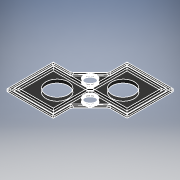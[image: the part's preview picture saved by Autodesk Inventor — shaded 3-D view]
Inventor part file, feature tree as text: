
AUTODESK INVENTOR PART (.ipt)
format: ipt  version: 2018 (Build 220112000, 112)  size: 885,248 bytes
history: native  units: mm
features: other x2, extrude x1, sketch x1
ambient origin geometry x8: Origin, YZ Plane, XZ Plane, XY Plane, X Axis, Y Axis, Z Axis, Center Point
bodies: Solid1 (feature_tree)
feature tree (4):
  other  "30mm_Parasitic_Element"
  other  "MeshFeature1"
  extrude  "Extrusion1"  Depth=2.62mm
  sketch  "Sketch1"  dims[d0=17.0mm d1=17.0mm d2=22.0mm d3=22.0mm d4=2.62mm d5=0.0mm]
